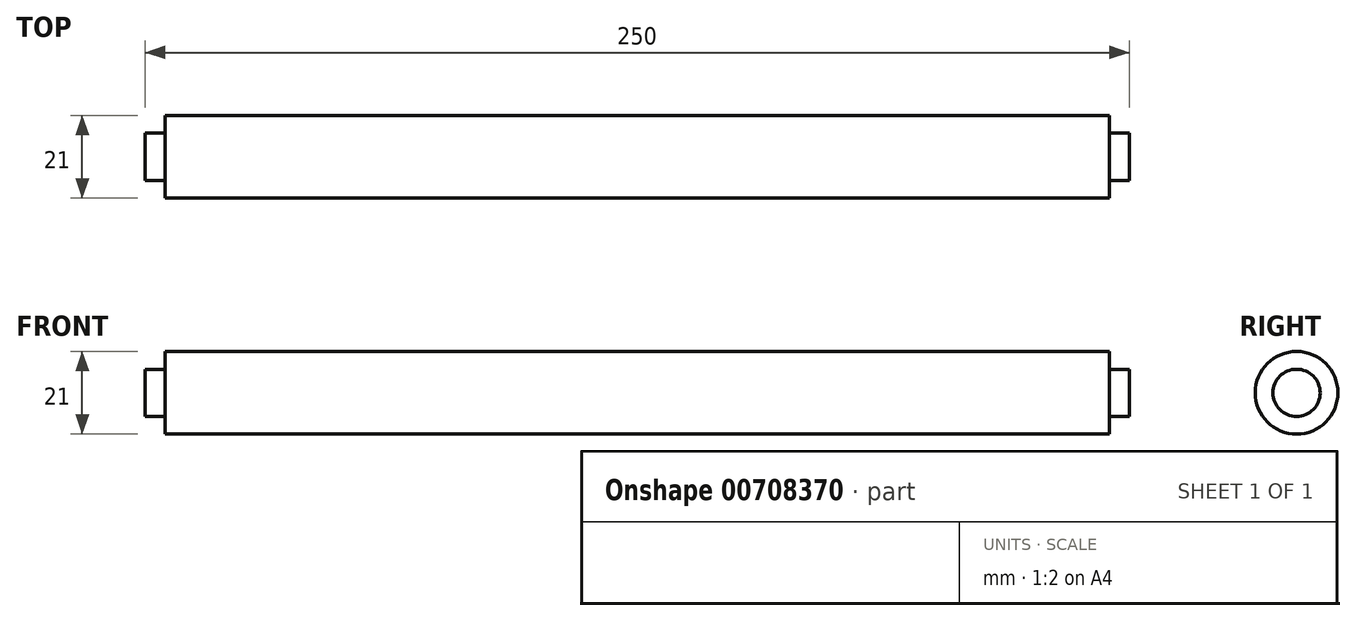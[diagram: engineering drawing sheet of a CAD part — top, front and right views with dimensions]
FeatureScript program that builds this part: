
annotation { "Feature Type Name" : "Feature", "Feature Type Description" : "" }
export const myFeature = defineFeature(function(context is Context, id is Id, definition is map)
    precondition{}
    {
        {
            var Q0;
            Q0=qCreatedBy(makeId("Right.planeOp"),FACE);
            var sketch = newSketch(context, id + "F0", { "sketchPlane" : qUnion([Q0])});
            skCircle(sketch, "E0", {"center": v(0, 0) * mm, "radius": 10.5 * mm});
            skSolve(sketch);
        }
        {
            var Q0;
            Q0 = qSketchRegion(id + "F0", true);
            extrude(context, id + "F1", {"entities" : qUnion([Q0]), "depth" : ((250 / 2) - 5) * mm, "offsetDistance" : 25 * mm});
        }
        {
            var Q0;
            Q0=makeQuery(id+"F1.opExtrude","CAP_FACE",FACE,{"disambiguationData":[OSD([sQuery(id+"F0.wireOp",EDGE,"E0")])],"isStart":false});
            var sketch = newSketch(context, id + "F2", { "sketchPlane" : qUnion([Q0])});
            skCircle(sketch, "E1", {"center": v(0, 0) * mm, "radius": 6 * mm});
            skSolve(sketch);
        }
        {
            var Q0;
            Q0=makeQuery(id+"F2.imprint","IMPRINT",FACE,{"disambiguationData":[TD([[makeQuery(id+"F2.imprint","IMPRINT",EDGE,{"derivedFrom":sQuery(id+"F2.wireOp",EDGE,"E1")}),1.0]])]});
            extrude(context, id + "F3", {"entities" : qUnion([Q0]), "operationType" : NewBodyOperationType.ADD, "depth" : 5 * mm, "offsetDistance" : 25 * mm});
        }
        {
            var Q0;
            Q0=makeQuery(id+"F1.opExtrude","SWEPT_BODY",BODY,{"disambiguationData":[OSD([sQuery(id+"F0.wireOp",EDGE,"E0")])]});
            var Q1;
            Q1=qCreatedBy(makeId("Right.planeOp"),FACE);
            mirror(context, id + "F4", {"operationType" : NewBodyOperationType.ADD, "entities" : qUnion([Q0]), "mirrorPlane" : qUnion([Q1])});
        }
    });
